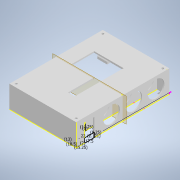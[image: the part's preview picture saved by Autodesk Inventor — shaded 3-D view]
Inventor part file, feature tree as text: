
AUTODESK INVENTOR PART (.ipt)
format: ipt  version: 2020.1 (Build 241239000, 239)  size: 654,336 bytes
history: native  units: mm
features: sketch x35, extrude x21, chamfer x2, hole x2, mirror x2, projected_geometry x2, plane x1
ambient origin geometry x8: Origin, YZ Plane, XZ Plane, XY Plane, X Axis, Y Axis, Z Axis, Center Point
bodies: Solid1 (feature_tree)
feature tree (65):
  extrude  "Extrusion1"  Depth=160.0mm
  extrude  "Extrusion2"  Depth=40.0mm
  sketch  "Sketch3"  dims[d2=40.0mm d3=0.0mm d4=60.0mm]
  extrude  "Extrusion3"  Depth=40.0mm
  extrude  "Extrusion4"  Depth=30.0mm
  sketch  "Sketch6"  dims[d9=30.0mm d10=30.0mm]
  extrude  "Extrusion5"  Depth=30.0mm
  extrude  "Extrusion10"  Depth=23.5mm
  sketch  "Sketch13"  dims[d18=160.0mm d19=2.4mm d20=0.0mm]
  extrude  "Extrusion11"  Depth=120.0mm
  sketch  "Sketch15"  dims[d26=25.0mm d27=23.0mm]
  extrude  "Extrusion12"  Depth=2.4mm TaperAngle=0.0deg
  sketch  "Sketch18"  dims[d45=4.0mm d46=0.0mm d47=5.0mm]
  sketch  "Sketch22"  dims[d48=160.0mm d49=36.0mm d50=0.0mm]
  extrude  "Extrusion17"  Depth=20.5mm
  sketch  "Sketch28"  dims[d69=49.0mm d70=3.5mm]
  sketch  "Sketch30"  dims[d71=20.0mm d72=6.0mm]
  sketch  "Sketch31"  dims[d73=6.0mm d74=6.0mm]
  extrude  "Extrusion21"  Depth=23.0mm
  sketch  "Sketch33"  dims[d75=6.0mm d76=8.0mm d77=0.0mm]
  sketch  "Sketch34"  dims[d78=2.75mm d79=2.75mm]
  extrude  "Extrusion30"  Depth=4.0mm TaperAngle=0.0deg
  extrude  "Extrusion31"  Depth=4.0mm
  extrude  "Extrusion32"  Depth=160.0mm TaperAngle=0.0deg
  extrude  "Extrusion33"  Depth=58.0mm
  sketch  "Sketch46"  dims[d103=4.0mm]
  extrude  "Extrusion34"  Depth=3.5mm
  extrude  "Extrusion35"  Depth=6.0mm
  sketch  "Sketch49"  dims[d129=1.0mm d158=1.5mm]
  extrude  "Extrusion36"  Depth=6.0mm
  plane  "Work Plane3"
  sketch  "Sketch52"  dims[d162=22.0mm]
  extrude  "Extrusion38"  Depth=6.0mm TaperAngle=0.0deg
  extrude  "Extrusion40"  Depth=2.75mm
  sketch  "Sketch56"  dims[d165=22.0mm d166=10.0mm d167=0.0mm]
  extrude  "Extrusion41"  Depth=2.75mm
  chamfer  "Chamfer2"  Distance=10.0mm
  sketch  "Sketch57"  dims[d168=8.05mm d169=1.6mm]
  hole  "Hole1"  [1 undecoded]
  mirror  "Mirror5"
  extrude  "Extrusion42"  Depth=1.5mm
  chamfer  "Chamfer3"  Distance=10.0mm
  hole  "Hole2"  [1 undecoded]
  mirror  "Mirror6"
  sketch  "Sketch2"  dims[d0=2.0mm d1=160.0mm]
  sketch  "Sketch4"  dims[d5=20.0mm d6=40.0mm]
  sketch  "Sketch5"  dims[d7=20.0mm d8=30.0mm]
  sketch  "Sketch7"  dims[d11=17.5mm d12=23.5mm]
  sketch  "Sketch12"  dims[d13=40.0mm d14=0.0mm d17=120.0mm]
  sketch  "Sketch14"  dims[d21=21.5mm d22=0.0mm d25=20.5mm]
  sketch  "Sketch16"  dims[d29=1.5mm d30=0.0mm d43=4.0mm d44=0.0mm]
  sketch  "Sketch23"  dims[d67=58.0mm d68=58.0mm]
  projected_geometry  "Projected Loop2"
  sketch  "Sketch42"  dims[d80=2.75mm d81=2.75mm]
  sketch  "Sketch43"  dims[d96=120.0mm]
  sketch  "Sketch44"  dims[d101=6.0mm]
  sketch  "Sketch45"  dims[d102=4.0mm]
  sketch  "Sketch47"  dims[d104=4.0mm]
  sketch  "Sketch48"  dims[d105=4.0mm d106=10.0mm d107=0.0mm]
  sketch  "Sketch50"  dims[d159=1.5mm d160=1.5mm]
  sketch  "Sketch53"  dims[d163=4.35mm]
  projected_geometry  "Projected Loop4"
  sketch  "Sketch55"  dims[d164=9.0mm]
  sketch  "Sketch58"  dims[d170=3.4mm]
  sketch  "Sketch59"  dims[d172=2.0mm d173=3.25mm d174=1.25mm d175=30.0mm d176=0.0mm d177=1.0mm d178=0.0mm d179=30.0mm d180=0.0mm d181=17.5mm d182=30.0mm d183=0.0mm d184=8.25mm d185=15.25mm d186=2.0mm d191=8.25mm d192=0.0mm d193=11.25mm d194=22.0mm d195=5.0mm d196=0.0mm d197=5.0mm d198=13.0mm d199=18.5mm d200=2.65mm d201=8.0mm d202=2.65mm d203=8.0mm d204=11.25mm d205=0.0mm d210=2.12132mm d211=1.5mm d212=10.0mm d213=0.0mm d225=40.0mm d226=53.0mm d227=41.0mm d228=25.419mm d229=12.0mm d230=39.0mm d231=10.0mm d232=0.0mm d233=0.0mm d235=1.2mm d236=6.0mm d237=4.0mm d238=18.0mm d239=10.0mm d240=10.0mm d241=0.0mm d242=6.0mm d243=2.0mm d244=45.0deg d245=4.0mm d246=6.0mm d247=8.4mm d248=2.0mm d249=90.0deg d250=10.0mm d251=20.594885mm d252=12.0mm d253=10.0mm d254=10.0mm d255=0.0mm d256=10.0mm d257=2.0mm d258=45.0deg d259=6.0mm d260=6.0mm d261=4.0mm d262=6.0mm d263=8.4mm d264=2.0mm d265=90.0deg d266=10.0mm d267=20.594885mm d15=0.5mm d16=0.872665mm d28=0.872665mm d35=0.5mm d36=0.872665mm d37=0.5mm d38=0.872665mm d83=0.5mm d84=0.872665mm d85=0.5mm d86=0.872665mm d98=0.5mm d99=0.872665mm d100=0.5mm d126=0.5mm d127=0.872665mm d128=0.5mm d148=0.5mm d149=0.872665mm d150=0.5mm d151=0.872665mm d152=0.5mm d153=0.872665mm d154=0.5mm d155=0.872665mm d268=0.75mm d269=20.594885mm d270=0.0625mm d271=0.75mm d272=0.375mm]
note: 2 required parameter values undecoded (feature->parameter linkage not recoverable at this tier; creation-order binding heuristic only, values carry confidence <= 0.55)
